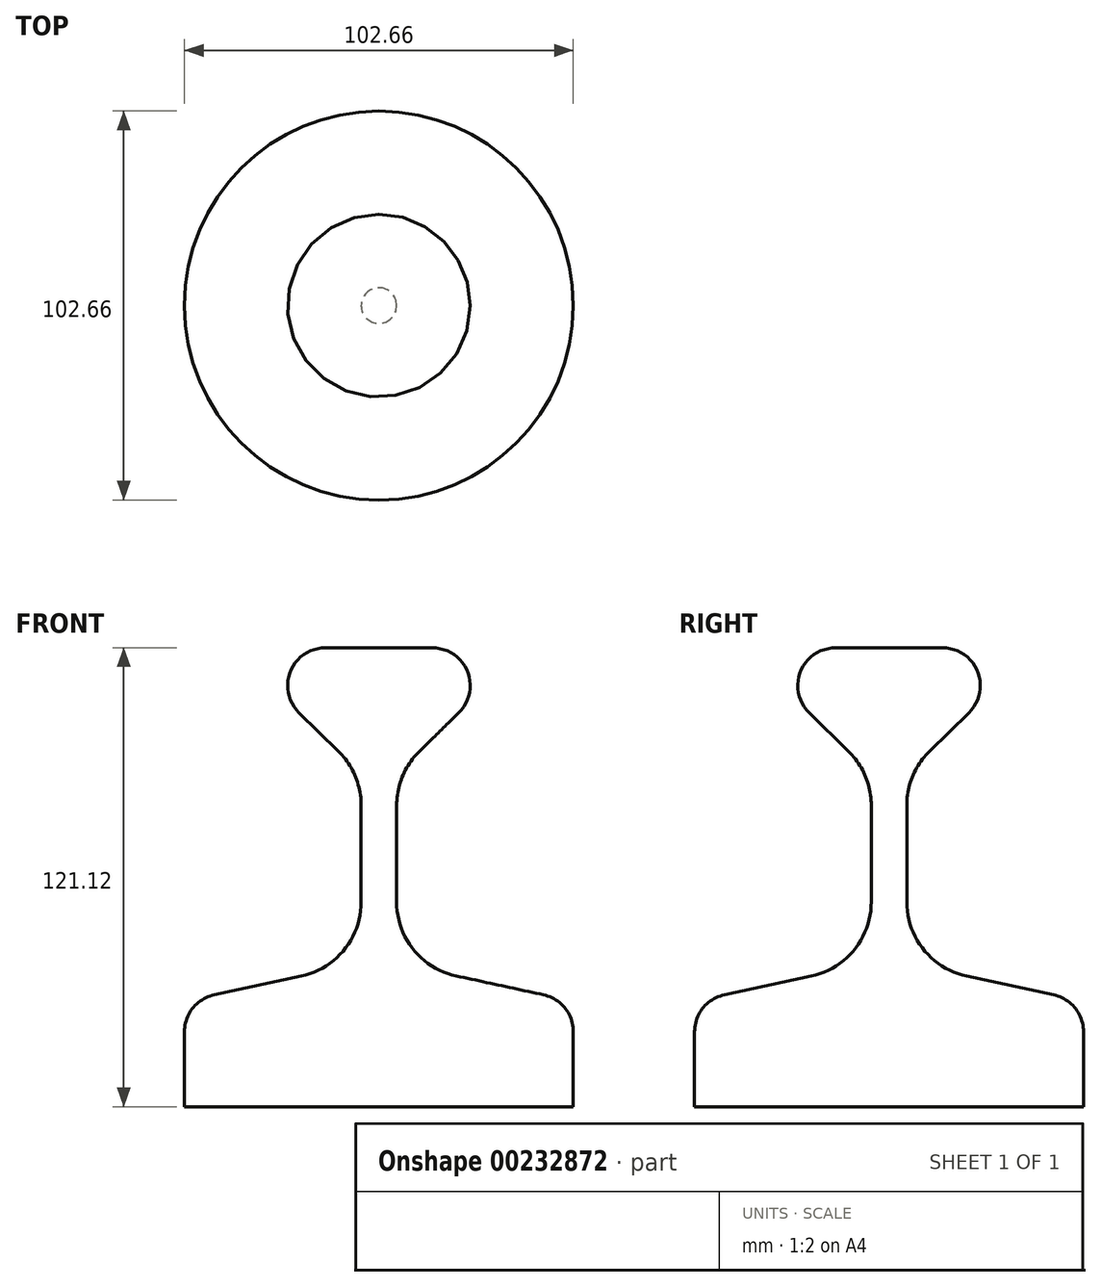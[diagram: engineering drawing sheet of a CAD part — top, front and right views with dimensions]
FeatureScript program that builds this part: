
annotation { "Feature Type Name" : "Feature", "Feature Type Description" : "" }
export const myFeature = defineFeature(function(context is Context, id is Id, definition is map)
    precondition{}
    {
        {
            var Q0;
            Q0=qCreatedBy(makeId("Right.planeOp"),FACE);
            var sketch = newSketch(context, id + "F0", { "sketchPlane" : qUnion([Q0])});
            skLineSegment(sketch, "E0", {"start": v(0, -73.76) * mm, "end": v(-51.33, -73.76) * mm});
            skLineSegment(sketch, "E1", {"start": v(-51.33, -73.76) * mm, "end": v(-51.33, -54) * mm});
            skLineSegment(sketch, "E2", {"start": v(-43.44, -44.22) * mm, "end": v(-20.47, -39.26) * mm});
            skLineSegment(sketch, "E3", {"start": v(-4.69, -19.7) * mm, "end": v(-4.69, 5.75) * mm});
            skLineSegment(sketch, "E4", {"start": v(-10.7, 20.04) * mm, "end": v(-21.09, 30.22) * mm});
            skLineSegment(sketch, "E5", {"start": v(-14.1, 47.36) * mm, "end": v(0, 47.36) * mm});
            skLineSegment(sketch, "E6", {"start": v(0, 47.36) * mm, "end": v(0, -73.76) * mm});
            skPoint(sketch, "E7.visualSharp", {"position": v(-4.69, -35.85) * mm});
            skArc(sketch, "E7.filletArc", {"start": v(-20.47, -39.26) * mm, "mid": v(-9.12, -32.27) * mm, "end": v(-4.69, -19.7) * mm});
            skPoint(sketch, "E8.visualSharp", {"position": v(-4.69, 14.16) * mm});
            skArc(sketch, "E8.filletArc", {"start": v(-4.69, 5.75) * mm, "mid": v(-6.25, 13.5) * mm, "end": v(-10.7, 20.04) * mm});
            skPoint(sketch, "E9.visualSharp", {"position": v(-51.33, -45.92) * mm});
            skArc(sketch, "E9.filletArc", {"start": v(-43.44, -44.22) * mm, "mid": v(-49.11, -47.71) * mm, "end": v(-51.33, -54) * mm});
            skPoint(sketch, "E10.visualSharp", {"position": v(-38.6, 47.36) * mm});
            skArc(sketch, "E10.filletArc", {"start": v(-14.1, 47.36) * mm, "mid": v(-23.35, 41.14) * mm, "end": v(-21.09, 30.22) * mm});
            skSolve(sketch);
        }
        {
            var Q0;
            Q0 = qSketchRegion(id + "F0", true);
            var Q1;
            Q1=sQuery(id+"F0.wireOp",EDGE,"E6");
            revolve(context, id + "F1", {"entities" : qUnion([Q0]), "axis" : qUnion([Q1]), "revolveType" : RevolveType.FULL});
        }
    });
